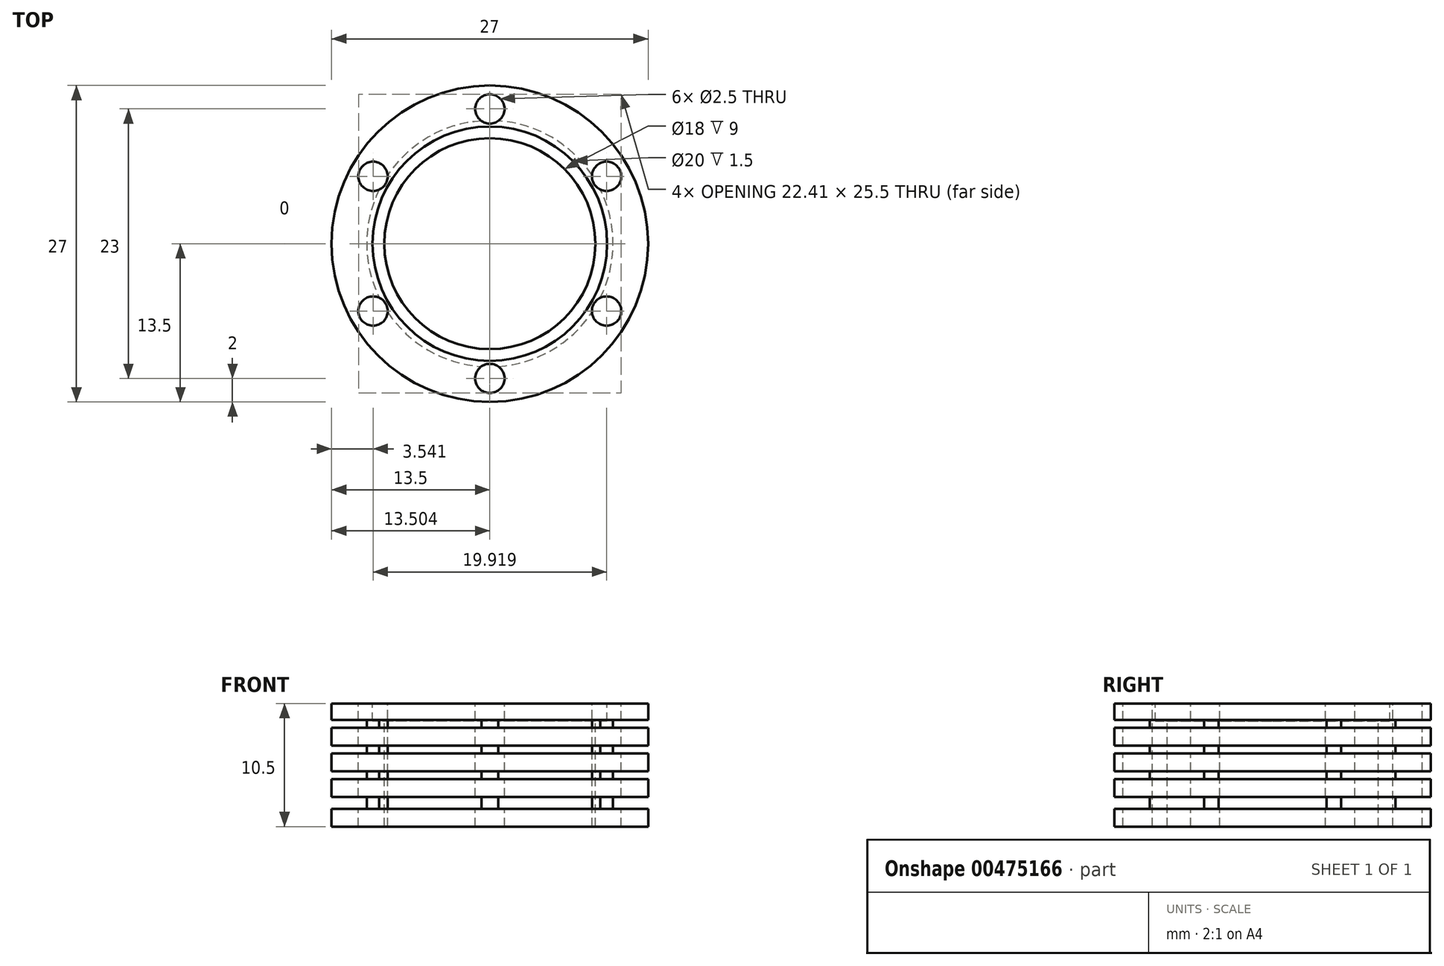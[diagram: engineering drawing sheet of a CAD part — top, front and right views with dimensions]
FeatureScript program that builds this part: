
annotation { "Feature Type Name" : "Feature", "Feature Type Description" : "" }
export const myFeature = defineFeature(function(context is Context, id is Id, definition is map)
    precondition{}
    {
        {
            var Q0;
            Q0=qCreatedBy(makeId("Front.planeOp"),FACE);
            var sketch = newSketch(context, id + "F0", { "sketchPlane" : qUnion([Q0])});
            skLineSegment(sketch, "E0", {"start": v(0, 24.47) * mm, "end": v(0, -24.47) * mm, "construction": true});
            skLineSegment(sketch, "E1", {"start": v(9, 0) * mm, "end": v(13.5, 0) * mm});
            skLineSegment(sketch, "E2", {"start": v(13.5, 0) * mm, "end": v(13.5, 1.52) * mm});
            skLineSegment(sketch, "E3", {"start": v(13.5, 1.52) * mm, "end": v(10.5, 1.52) * mm});
            skLineSegment(sketch, "E4", {"start": v(10.5, 1.52) * mm, "end": v(10.5, 2.52) * mm});
            skLineSegment(sketch, "E5", {"start": v(10.5, 2.52) * mm, "end": v(13.5, 2.52) * mm});
            skLineSegment(sketch, "E6", {"start": v(13.5, 2.52) * mm, "end": v(13.5, 4.05) * mm});
            skLineSegment(sketch, "E7", {"start": v(13.5, 4.05) * mm, "end": v(10.5, 4.05) * mm});
            skLineSegment(sketch, "E8", {"start": v(10.5, 4.05) * mm, "end": v(10.5, 4.72) * mm});
            skLineSegment(sketch, "E9", {"start": v(10.5, 4.72) * mm, "end": v(13.5, 4.72) * mm});
            skLineSegment(sketch, "E10", {"start": v(13.5, 4.72) * mm, "end": v(13.5, 6.24) * mm});
            skLineSegment(sketch, "E11", {"start": v(13.5, 6.24) * mm, "end": v(10.5, 6.24) * mm});
            skLineSegment(sketch, "E12", {"start": v(10.5, 6.24) * mm, "end": v(10.5, 6.9) * mm});
            skLineSegment(sketch, "E13", {"start": v(10.5, 6.9) * mm, "end": v(13.5, 6.9) * mm});
            skLineSegment(sketch, "E14", {"start": v(13.5, 6.9) * mm, "end": v(13.5, 8.43) * mm});
            skLineSegment(sketch, "E15", {"start": v(13.5, 8.43) * mm, "end": v(10.5, 8.43) * mm});
            skLineSegment(sketch, "E16", {"start": v(10.5, 8.43) * mm, "end": v(10.5, 9.1) * mm});
            skLineSegment(sketch, "E17", {"start": v(10.5, 9.1) * mm, "end": v(13.5, 9.1) * mm});
            skLineSegment(sketch, "E18", {"start": v(13.5, 9.1) * mm, "end": v(13.5, 10.5) * mm});
            skLineSegment(sketch, "E19", {"start": v(13.5, 10.5) * mm, "end": v(10, 10.5) * mm});
            skLineSegment(sketch, "E20", {"start": v(10, 10.5) * mm, "end": v(10, 9) * mm});
            skLineSegment(sketch, "E21", {"start": v(10, 9) * mm, "end": v(9, 9) * mm});
            skLineSegment(sketch, "E22", {"start": v(9, 9) * mm, "end": v(9, 0) * mm});
            skSolve(sketch);
        }
        {
            var Q0;
            Q0=makeQuery(id+"F0.imprint","IMPRINT",FACE,{"disambiguationData":[TD([[makeQuery(id+"F0.imprint","IMPRINT",EDGE,{"derivedFrom":sQuery(id+"F0.wireOp",EDGE,"E1")}),1.0]])]});
            var Q1;
            Q1=sQuery(id+"F0.wireOp",EDGE,"E0");
            revolve(context, id + "F1", {"entities" : qUnion([Q0]), "axis" : qUnion([Q1]), "revolveType" : RevolveType.FULL});
        }
        {
            var Q0;
            Q0=makeQuery(id+"F1.opRevolve","SWEPT_FACE",FACE,{"disambiguationData":[OSD([sQuery(id+"F0.wireOp",EDGE,"E19")])]});
            var sketch = newSketch(context, id + "F2", { "sketchPlane" : qUnion([Q0])});
            skCircle(sketch, "E23", {"center": v(0, 0) * mm, "radius": 11.5 * mm, "construction": true});
            skLineSegment(sketch, "E24", {"start": v(0, 0) * mm, "end": v(21.28, 0) * mm, "construction": true});
            skLineSegment(sketch, "E25", {"start": v(0, 0) * mm, "end": v(12.95, 7.48) * mm, "construction": true});
            skCircle(sketch, "E26", {"center": v(9.96, 5.75) * mm, "radius": 1.25 * mm});
            skCircle(sketch, "E27.1.0", {"center": v(0, 11.5) * mm, "radius": 1.25 * mm});
            skCircle(sketch, "E27.2.0", {"center": v(-9.96, 5.75) * mm, "radius": 1.25 * mm});
            skCircle(sketch, "E27.3.0", {"center": v(-9.96, -5.75) * mm, "radius": 1.25 * mm});
            skCircle(sketch, "E27.4.0", {"center": v(0, -11.5) * mm, "radius": 1.25 * mm});
            skCircle(sketch, "E27.5.0", {"center": v(9.96, -5.75) * mm, "radius": 1.25 * mm});
            skSolve(sketch);
        }
        {
            var Q0;
            Q0=makeQuery(id+"F2.imprint","IMPRINT",FACE,{"disambiguationData":[TD([[makeQuery(id+"F2.imprint","IMPRINT",EDGE,{"derivedFrom":sQuery(id+"F2.wireOp",EDGE,"E27.1.0")}),1.0]])]});
            var Q1;
            Q1=makeQuery(id+"F2.imprint","IMPRINT",FACE,{"disambiguationData":[TD([[makeQuery(id+"F2.imprint","IMPRINT",EDGE,{"derivedFrom":sQuery(id+"F2.wireOp",EDGE,"E27.2.0")}),1.0]])]});
            var Q2;
            Q2=makeQuery(id+"F2.imprint","IMPRINT",FACE,{"disambiguationData":[TD([[makeQuery(id+"F2.imprint","IMPRINT",EDGE,{"derivedFrom":sQuery(id+"F2.wireOp",EDGE,"E27.3.0")}),1.0]])]});
            var Q3;
            Q3=makeQuery(id+"F2.imprint","IMPRINT",FACE,{"disambiguationData":[TD([[makeQuery(id+"F2.imprint","IMPRINT",EDGE,{"derivedFrom":sQuery(id+"F2.wireOp",EDGE,"E27.4.0")}),1.0]])]});
            var Q4;
            Q4=makeQuery(id+"F2.imprint","IMPRINT",FACE,{"disambiguationData":[TD([[makeQuery(id+"F2.imprint","IMPRINT",EDGE,{"derivedFrom":sQuery(id+"F2.wireOp",EDGE,"E27.5.0")}),1.0]])]});
            var Q5;
            Q5=makeQuery(id+"F2.imprint","IMPRINT",FACE,{"disambiguationData":[TD([[makeQuery(id+"F2.imprint","IMPRINT",EDGE,{"derivedFrom":sQuery(id+"F2.wireOp",EDGE,"E26")}),1.0]])]});
            extrude(context, id + "F3", {"entities" : qUnion([Q0, Q1, Q2, Q3, Q4, Q5]), "operationType" : NewBodyOperationType.REMOVE, "oppositeDirection" : true, "depth" : 25 * mm});
        }
    });
